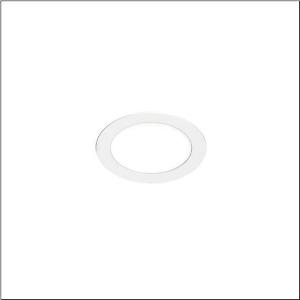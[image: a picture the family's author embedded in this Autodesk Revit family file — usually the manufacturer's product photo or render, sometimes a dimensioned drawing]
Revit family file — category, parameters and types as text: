
# Revit family: lunis_41_flat_51dr10ddgbb
name_source: partatom
category: Lighting Fixtures
units: mm (PartAtom-declared; Revit-internal decimal feet)

## family parameters
Cut with Voids When Loaded = No
Host = Face
Light Source = No
Part Type = Normal
Room Calculation Point = No
Round Connector Dimension = Use Diameter
Shared = No

## types (1)
- --- (1 x LED, 1750 lm, 14 W, 4000K)
    Apparent Load = 14 VA
    CIE Flux Codes = 49 80 96 100 100
    Color Rendering = 80
    Color Temperature = 4000K
    Default Elevation = 1800 mm
    Description = Lunis 41 Flat, downlight, light emission: direct distribution, LED rated luminous flux: 1.750lm, light colour: 830/840, control gear: ECG, mains connection: 230V, AC, 50/60Hz, housing, round, of aluminium, coated, traffic white (RAL 9016), diameter: 170mm, protection rating (complete): IP20, protection rating (on room side): IP44, insulation class (complete): insulation class II (safety insulation), certification: CE, permissible ambient temperature for indoor applications: -20..+40°C, packaging unit: 1 piece
    Height = 0 mm  [stored 0 ft]
    Lamp = 1 x LED
    Lamp Light Flux = 1750 lm
    Lamp Power = 14 W
    Lamp count = 1
    Length = 170 mm  [stored 0.557743 ft]
    Luminous efficacy = 125 lm/W
    Manufacturer = Siteco
    ModVariant = No
    Model = 51DR10DDGBB
    Mounting Place = Ceiling
    Mounting Type = Recessed
    Number of Poles = 1
    OnlyDefault = Yes
    Power Factor = 1
    Product Name = Lunis 41 Flat
    Product group = downlight
    ProductGroupID = 401
    Protection Class = Protection class II
    Protection Degree = IP 20
    RLX_Detail_Level = 1
    RLX_Emergency_Light_Flux = 0 lm
    RLX_Emergency_Type = 0
    RLX_Emergency_Type_DB = No
    RlxData = <blob elided: 10881 chars, md5=f313364c>
    Socket = socket
    Standby Power = 0 W
    System Light Flux = 1750 lm
    System Power = 14 W
    Type Comments = factory setting: colour temperature 4000K, luminous flux: 100 % | (ON | ON) | 350 mA
    Type Image = l_1340921.jpg
    URL = http://relux.com
    VarID = @adj_021575
    Voltage = 0 V
    Weight = 0.00 kg
    Width = 0 mm  [stored 0 ft]

note: [stored X ft] marks values corroborated as IEEE doubles in the binary element streams (Revit-internal decimal feet)

## geometry (parser evidence)
native form markers: Sweep x8
no freeform markers — native parametric forms only
